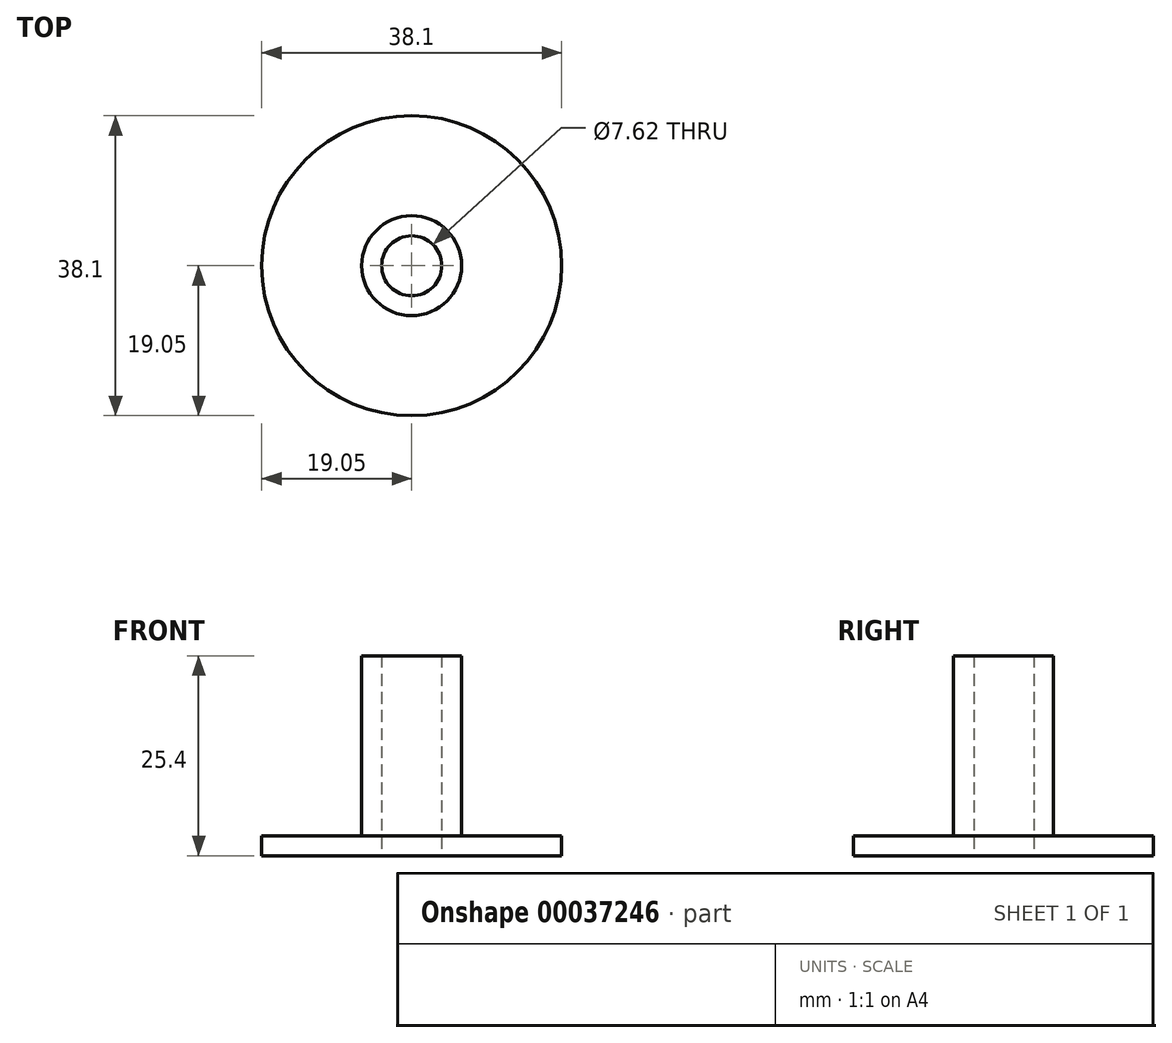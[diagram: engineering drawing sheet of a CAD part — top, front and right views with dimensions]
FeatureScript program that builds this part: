
annotation { "Feature Type Name" : "Feature", "Feature Type Description" : "" }
export const myFeature = defineFeature(function(context is Context, id is Id, definition is map)
    precondition{}
    {
        {
            var Q0;
            Q0=qCreatedBy(makeId("Top.planeOp"),FACE);
            var sketch = newSketch(context, id + "F0", { "sketchPlane" : qUnion([Q0])});
            skCircle(sketch, "E0", {"center": v(0, 0) * mm, "radius": 19.05 * mm});
            skCircle(sketch, "E1", {"center": v(0, 0) * mm, "radius": 6.35 * mm});
            skCircle(sketch, "E2", {"center": v(0, 0) * mm, "radius": 3.81 * mm});
            skSolve(sketch);
        }
        {
            var Q0;
            Q0=makeQuery(id+"F0.imprint","IMPRINT",FACE,{"disambiguationData":[TD([[makeQuery(id+"F0.imprint","IMPRINT",EDGE,{"derivedFrom":sQuery(id+"F0.wireOp",EDGE,"E1")}),1.0]])]});
            extrude(context, id + "F1", {"entities" : qUnion([Q0]), "depth" : 25.4 * mm});
        }
        {
            var Q0;
            Q0=makeQuery(id+"F0.imprint","IMPRINT",FACE,{"disambiguationData":[TD([[makeQuery(id+"F0.imprint","IMPRINT",EDGE,{"derivedFrom":sQuery(id+"F0.wireOp",EDGE,"E0")}),1.0]])]});
            extrude(context, id + "F2", {"entities" : qUnion([Q0]), "operationType" : NewBodyOperationType.ADD, "depth" : 2.54 * mm});
        }
    });
